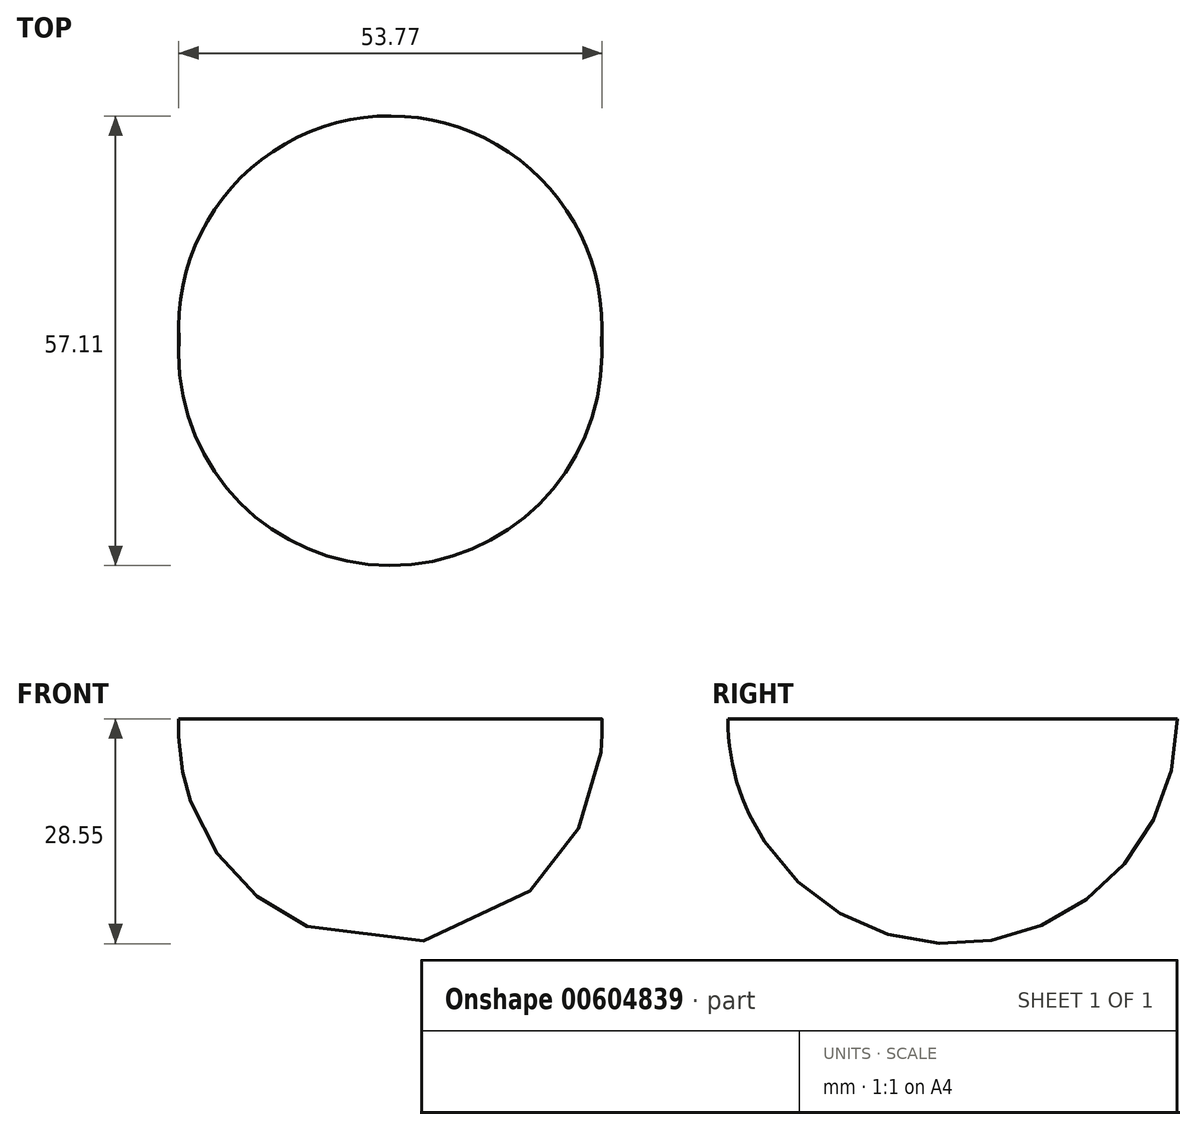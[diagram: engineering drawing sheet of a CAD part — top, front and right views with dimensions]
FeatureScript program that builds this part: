
annotation { "Feature Type Name" : "Feature", "Feature Type Description" : "" }
export const myFeature = defineFeature(function(context is Context, id is Id, definition is map)
    precondition{}
    {
        {
            var Q0;
            Q0=qCreatedBy(makeId("Top.planeOp"),FACE);
            var sketch = newSketch(context, id + "F0", { "sketchPlane" : qUnion([Q0])});
            skArc(sketch, "E0", {"start": v(-26.82, -0.7) * mm, "mid": v(-0.07, -29.32) * mm, "end": v(26.83, -0.84) * mm});
            skLineSegment(sketch, "E1", {"start": v(-26.82, -0.7) * mm, "end": v(26.83, -0.84) * mm});
            skSolve(sketch);
        }
        {
            var Q0;
            Q0=makeQuery(id+"F0.imprint","IMPRINT",FACE,{"disambiguationData":[TD([[makeQuery(id+"F0.imprint","IMPRINT",EDGE,{"derivedFrom":sQuery(id+"F0.wireOp",EDGE,"E0")}),1.0]])]});
            var Q1;
            Q1=sQuery(id+"F0.wireOp",EDGE,"E1");
            revolve(context, id + "F1", {"entities" : qUnion([Q0]), "axis" : qUnion([Q1]), "revolveType" : RevolveType.ONE_DIRECTION, "angle" : 180 * degree});
        }
    });
